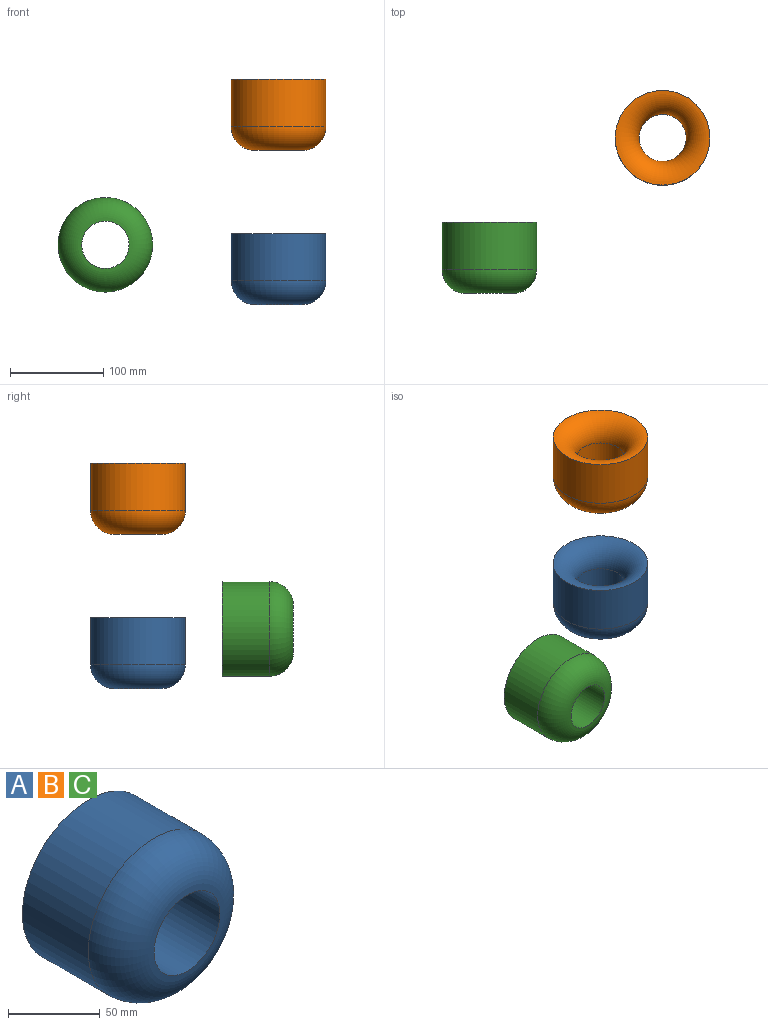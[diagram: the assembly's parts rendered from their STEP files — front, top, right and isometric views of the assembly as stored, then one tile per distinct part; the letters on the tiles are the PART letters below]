
ASSEMBLY  parts=3 mates=1
PART A: 4 faces, bbox 149x76.2x149 mm
  f0: cylinder r=50.8mm len=101.6mm, axis (0,1,0), area 16214.6mm2, adj f1,f3
  f1: torus R=25.4mm, axis (0,-1,0), area 10421.1mm2, adj f0,f2
  f2: cylinder r=25.4mm len=50.8mm, axis (0,-1,0), area 8107.3mm2, adj f1,f3
  f3: torus R=50.8mm, axis (0,-1,0), area 8681.3mm2, adj f0,f2
PART B: same geometry as A
PART C: same geometry as A
PLACE A rot(axis=(0.98,0.13,0.13),91deg) t=(0,0,37.21)mm fixed
PLACE B rot(axis=(0.93,-0.26,-0.26),94deg) t=(0,0,202.76)mm
PLACE C t=(-186.05,-90.64,25.17)mm
MATE cylindrical B.f0 <-> A.f0  axis (0,0,1) through (0,0,202.76)mm
